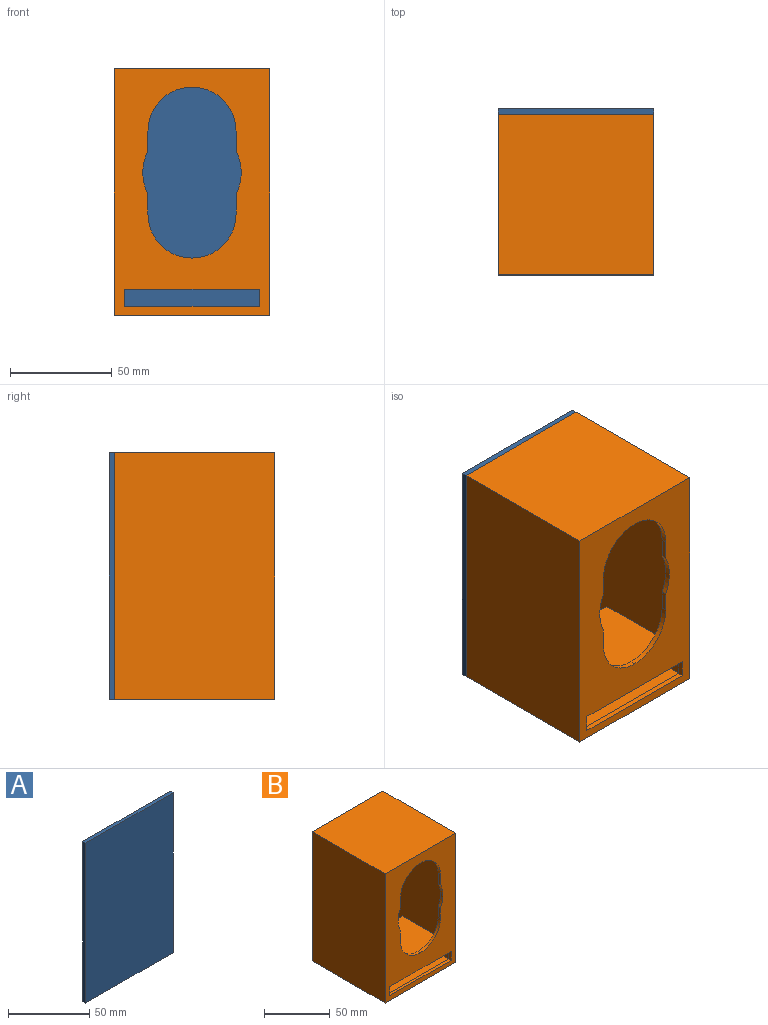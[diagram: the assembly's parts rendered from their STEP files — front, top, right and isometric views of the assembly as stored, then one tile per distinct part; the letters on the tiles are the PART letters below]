
ASSEMBLY  parts=2 mates=1
PART A: 6 faces, bbox 76.2x2.5x120.7 mm
  f0: plane 76.2x2.54mm, normal (0,0,1), area 193.5mm2, adj f1,f3,f4,f5
  f1: plane 120.65x2.54mm, normal (-1,0,0), area 306.5mm2, adj f0,f2,f4,f5
  f2: plane 76.2x2.54mm, normal (0,0,-1), area 193.5mm2, adj f1,f3,f4,f5
  f3: plane 120.65x2.54mm, normal (1,0,0), area 306.5mm2, adj f0,f2,f4,f5
  f4: plane 120.65x76.2mm, normal (0,-1,0), area 9193.5mm2, adj f0,f1,f2,f3
  f5: plane 120.65x76.2mm, normal (0,1,0), area 9193.5mm2, adj f0,f1,f2,f3
PART B: 31 faces, bbox 76.2x78.7x120.7 mm
  f0: plane 120.65x76.2mm, normal (0,-1,0), area 5346.3mm2, adj f5,f6,f7,f8,f9,f10,f11,f12
  f1: plane 69.08x12.71mm, normal (0,1,0), area 325.2mm2, adj f3,f4,f22,f25,f27,f28,f29,f30
  f2: plane 98.46x69.08mm, normal (0,1,0), area 3507.3mm2, adj f3,f4,f8,f9,f10,f11,f12,f13
  f3: plane 113.71x76.2mm, normal (-1,0,0), area 8535.9mm2, adj f1,f2,f21,f22,f23,f24,f25,f26
  f4: plane 113.71x76.2mm, normal (1,0,0), area 8535.9mm2, adj f1,f2,f21,f22,f23,f24,f25,f26
  f5: plane 78.74x76.2mm, normal (0,0,1), area 6000mm2, adj f0,f6,f20,f23
  f6: plane 120.65x78.74mm, normal (-1,0,0), area 9500mm2, adj f0,f5,f7,f23
  f7: plane 78.74x76.2mm, normal (0,0,-1), area 6000mm2, adj f0,f6,f20,f23
  f8: plane 9.58x2.54mm, normal (1,0,0), area 24.3mm2, adj f0,f2,f9,f19
  f9: cylinder r=24.13mm len=21.55mm, axis (0,1,0), area 56.7mm2, adj f0,f2,f8,f10
  f10: plane 9.58x2.54mm, normal (1,0,0), area 24.3mm2, adj f0,f2,f9,f11
  f11: cylinder r=21.55mm len=21.55mm, axis (0,1,0), area 86mm2, adj f0,f2,f10,f12
  f12: plane 2.54x0.08mm, normal (0,0,-1), area 0.2mm2, adj f0,f2,f11,f13
  f13: cylinder r=21.55mm len=21.55mm, axis (0,1,0), area 86mm2, adj f0,f2,f12,f14
  f14: plane 9.58x2.54mm, normal (-1,0,0), area 24.3mm2, adj f0,f2,f13,f15
  f15: cylinder r=24.13mm len=21.55mm, axis (0,1,0), area 56.7mm2, adj f0,f2,f14,f16
  f16: plane 9.58x2.54mm, normal (-1,0,0), area 24.3mm2, adj f0,f2,f15,f17
  f17: cylinder r=21.55mm len=21.55mm, axis (0,1,0), area 86mm2, adj f0,f2,f16,f18
  f18: plane 2.54x0.08mm, normal (0,0,1), area 0.2mm2, adj f0,f2,f17,f19
  f19: cylinder r=21.55mm len=21.55mm, axis (0,1,0), area 86mm2, adj f0,f2,f8,f18
  f20: plane 120.65x78.74mm, normal (1,0,0), area 9500mm2, adj f0,f5,f7,f23
  f21: plane 76.2x69.08mm, normal (0,0,-1), area 5263.7mm2, adj f2,f3,f4,f23
  f22: plane 76.2x69.08mm, normal (0,0,1), area 5263.7mm2, adj f1,f3,f4,f23
  f23: plane 120.65x76.2mm, normal (0,1,0), area 1338.4mm2, adj f3,f4,f5,f6,f7,f20,f21,f22
  f24: plane 69.08x2.54mm, normal (0,1,0), area 175.5mm2, adj f3,f4,f25,f26
  f25: plane 69.08x50.8mm, normal (0,0,-1), area 3509.2mm2, adj f1,f3,f4,f24
  f26: plane 69.08x50.8mm, normal (0,0,1), area 3509.2mm2, adj f2,f3,f4,f24
  f27: plane 66.04x2.54mm, normal (0,0,-1), area 167.7mm2, adj f0,f1,f28,f30
  f28: plane 8.37x2.54mm, normal (1,0,0), area 21.3mm2, adj f0,f1,f27,f29
  f29: plane 66.04x2.54mm, normal (0,0,1), area 167.7mm2, adj f0,f1,f28,f30
  f30: plane 8.37x2.54mm, normal (-1,0,0), area 21.3mm2, adj f0,f1,f27,f29
PLACE A t=(-2.19,41.8,20.48)mm
PLACE B t=(41.19,-36.94,28.87)mm
MATE fastened B.f23 <-> A.f4  axis (0,1,0) through (-9.61,39.26,80.15)mm
